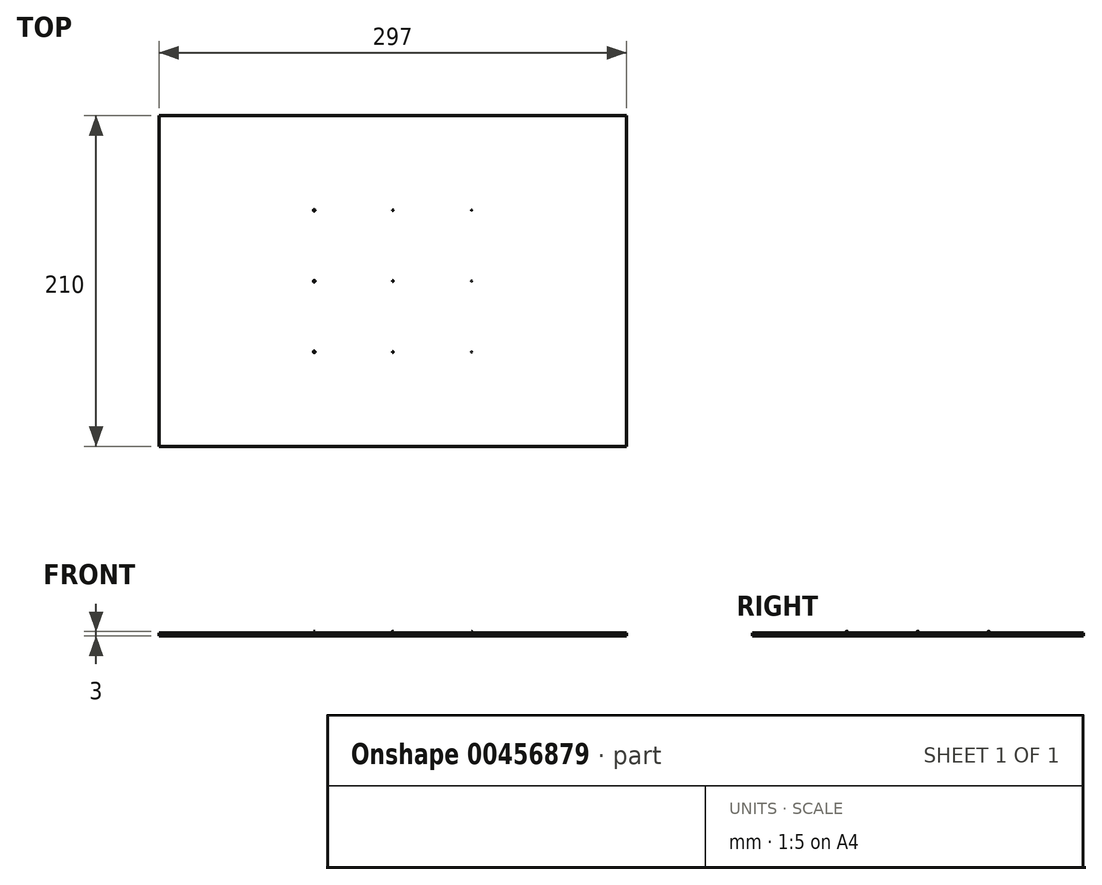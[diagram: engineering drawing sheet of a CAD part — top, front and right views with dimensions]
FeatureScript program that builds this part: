
annotation { "Feature Type Name" : "Feature", "Feature Type Description" : "" }
export const myFeature = defineFeature(function(context is Context, id is Id, definition is map)
    precondition{}
    {
        {
            var Q0;
            Q0=qCreatedBy(makeId("Top.planeOp"),FACE);
            var sketch = newSketch(context, id + "F0", { "sketchPlane" : qUnion([Q0])});
            skLineSegment(sketch, "E0.bottom", {"start": v(-148.5, 105) * mm, "end": v(148.5, 105) * mm});
            skLineSegment(sketch, "E0.top", {"start": v(-148.5, -105) * mm, "end": v(148.5, -105) * mm});
            skLineSegment(sketch, "E0.left", {"start": v(-148.5, 105) * mm, "end": v(-148.5, -105) * mm});
            skLineSegment(sketch, "E0.right", {"start": v(148.5, 105) * mm, "end": v(148.5, -105) * mm});
            skPoint(sketch, "E0.middle", {"position": v(0, 0) * mm});
            skSolve(sketch);
        }
        {
            var Q0;
            Q0 = qSketchRegion(id + "F0", true);
            extrude(context, id + "F1", {"entities" : qUnion([Q0]), "depth" : 2 * mm});
        }
        {
            var Q0;
            Q0=makeQuery(id+"F1.opExtrude","CAP_FACE",FACE,{"disambiguationData":[OSD([sQuery(id+"F0.wireOp",EDGE,"E0.bottom"),sQuery(id+"F0.wireOp",EDGE,"E0.top"),sQuery(id+"F0.wireOp",EDGE,"E0.left"),sQuery(id+"F0.wireOp",EDGE,"E0.right")])],"isStart":false});
            var sketch = newSketch(context, id + "F2", { "sketchPlane" : qUnion([Q0])});
            skCircle(sketch, "E1", {"center": v(50, 45) * mm, "radius": 0.1 * mm});
            skCircle(sketch, "E2", {"center": v(50, 0) * mm, "radius": 0.1 * mm});
            skCircle(sketch, "E3", {"center": v(50, -45) * mm, "radius": 0.1 * mm});
            skSolve(sketch);
        }
        {
            var Q0;
            Q0 = qSketchRegion(id + "F2", true);
            extrude(context, id + "F3", {"entities" : qUnion([Q0]), "operationType" : NewBodyOperationType.ADD, "depth" : 1 * mm});
        }
        {
            var Q0;
            Q0=makeQuery(id+"F1.opExtrude","CAP_FACE",FACE,{"disambiguationData":[OSD([sQuery(id+"F0.wireOp",EDGE,"E0.bottom"),sQuery(id+"F0.wireOp",EDGE,"E0.top"),sQuery(id+"F0.wireOp",EDGE,"E0.left"),sQuery(id+"F0.wireOp",EDGE,"E0.right")])],"isStart":false});
            var sketch = newSketch(context, id + "F4", { "sketchPlane" : qUnion([Q0])});
            skCircle(sketch, "E4", {"center": v(0, 45) * mm, "radius": 0.25 * mm});
            skCircle(sketch, "E5", {"center": v(0, 0) * mm, "radius": 0.25 * mm});
            skCircle(sketch, "E6", {"center": v(0, -45) * mm, "radius": 0.25 * mm});
            skSolve(sketch);
        }
        {
            var Q0;
            Q0 = qSketchRegion(id + "F4", true);
            extrude(context, id + "F5", {"entities" : qUnion([Q0]), "operationType" : NewBodyOperationType.ADD, "depth" : 1 * mm});
        }
        {
            var Q0;
            Q0=makeQuery(id+"F1.opExtrude","CAP_FACE",FACE,{"disambiguationData":[OSD([sQuery(id+"F0.wireOp",EDGE,"E0.bottom"),sQuery(id+"F0.wireOp",EDGE,"E0.top"),sQuery(id+"F0.wireOp",EDGE,"E0.left"),sQuery(id+"F0.wireOp",EDGE,"E0.right")])],"isStart":false});
            var sketch = newSketch(context, id + "F6", { "sketchPlane" : qUnion([Q0])});
            skCircle(sketch, "E7", {"center": v(-50, 45) * mm, "radius": 0.5 * mm});
            skCircle(sketch, "E8", {"center": v(-50, 0) * mm, "radius": 0.5 * mm});
            skCircle(sketch, "E9", {"center": v(-50, -45) * mm, "radius": 0.5 * mm});
            skSolve(sketch);
        }
        {
            var Q0;
            Q0 = qSketchRegion(id + "F6", true);
            extrude(context, id + "F7", {"entities" : qUnion([Q0]), "operationType" : NewBodyOperationType.ADD, "depth" : 1 * mm});
        }
    });
